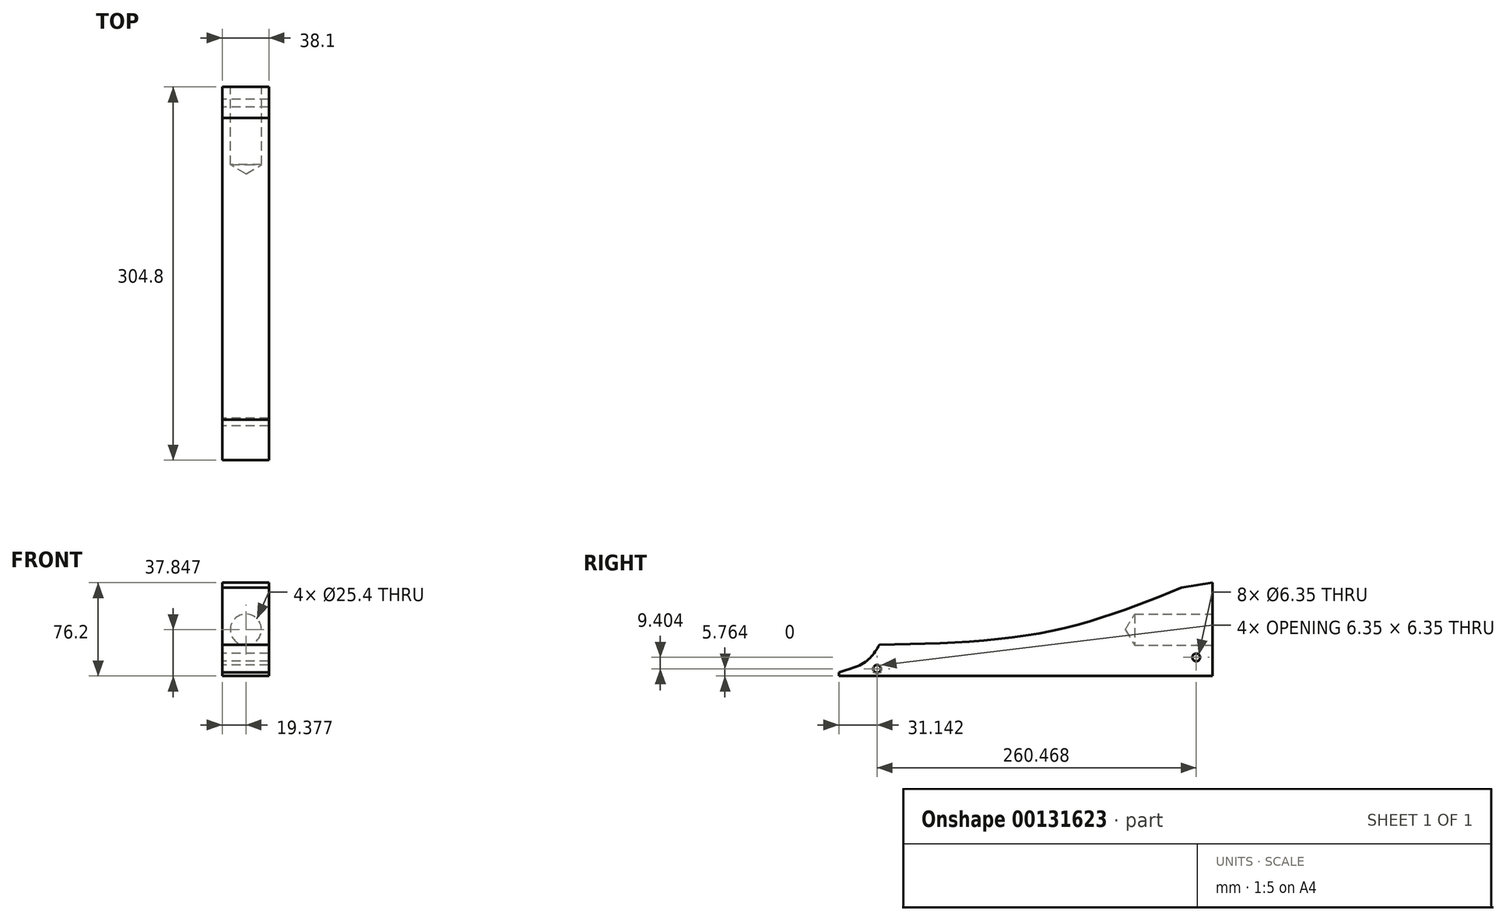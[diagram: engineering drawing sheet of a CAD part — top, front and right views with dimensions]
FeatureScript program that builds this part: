
annotation { "Feature Type Name" : "Feature", "Feature Type Description" : "" }
export const myFeature = defineFeature(function(context is Context, id is Id, definition is map)
    precondition{}
    {
        {
            var Q0;
            Q0=qCreatedBy(makeId("Right.planeOp"),FACE);
            var sketch = newSketch(context, id + "F0", { "sketchPlane" : qUnion([Q0])});
            skLineSegment(sketch, "E0", {"start": v(-61.93, -29.35) * mm, "end": v(-61.93, -54.75) * mm});
            skLineSegment(sketch, "E1", {"start": v(-61.93, -54.75) * mm, "end": v(242.87, -54.75) * mm});
            skLineSegment(sketch, "E2", {"start": v(242.87, -54.75) * mm, "end": v(242.87, 21.45) * mm});
            skLineSegment(sketch, "E3", {"start": v(242.87, 21.45) * mm, "end": v(-61.93, -29.35) * mm});
            skSolve(sketch);
        }
        {
            var Q0;
            Q0=makeQuery(id+"F0.imprint","IMPRINT",FACE,{"disambiguationData":[TD([[makeQuery(id+"F0.imprint","IMPRINT",EDGE,{"derivedFrom":sQuery(id+"F0.wireOp",EDGE,"E0")}),1.0]])]});
            extrude(context, id + "F1", {"entities" : qUnion([Q0]), "endBound" : BoundingType.SYMMETRIC, "depth" : 38.1 * mm});
        }
        {
            var Q0;
            Q0=makeQuery(id+"F1.opExtrude","SWEPT_FACE",FACE,{"disambiguationData":[OSD([sQuery(id+"F0.wireOp",EDGE,"E2")])]});
            var sketch = newSketch(context, id + "F2", { "sketchPlane" : qUnion([Q0])});
            skPoint(sketch, "E4", {"position": v(-0.33, -16.9) * mm});
            skSolve(sketch);
        }
        {
            var Q0;
            Q0=sQuery(id+"F2.wireOp",VERTEX,"E4");
            var Q1;
            Q1=makeQuery(id+"F1.opExtrude","SWEPT_BODY",BODY,{"disambiguationData":[OSD([sQuery(id+"F0.wireOp",EDGE,"E0"),sQuery(id+"F0.wireOp",EDGE,"E1"),sQuery(id+"F0.wireOp",EDGE,"E2"),sQuery(id+"F0.wireOp",EDGE,"E3")])]});
            hole(context, id + "F3", {"style" : HoleStyle.SIMPLE, "endStyle" : HoleEndStyle.BLIND, "holeDiameter" : 25.4 * mm, "holeDepth" : 63.5 * mm, "locations" : qUnion([Q0]), "scope" : qUnion([Q1])});
        }
        {
            var Q0;
            Q0=makeQuery(id+"F1.opExtrude","CAP_FACE",FACE,{"disambiguationData":[OSD([sQuery(id+"F0.wireOp",EDGE,"E0"),sQuery(id+"F0.wireOp",EDGE,"E1"),sQuery(id+"F0.wireOp",EDGE,"E2"),sQuery(id+"F0.wireOp",EDGE,"E3")])],"isStart":true});
            var sketch = newSketch(context, id + "F4", { "sketchPlane" : qUnion([Q0])});
            skFitSpline(sketch, "E5", {"points": [v(-217.43, 17.21) * mm, v(-104.02, -19.52) * mm, v(61.93, -29.35) * mm], "startDerivative": vector(233.78, -94.31) * mm, "endDerivative": vector(322.5, -1.38) * mm});
            skSolve(sketch);
        }
        {
            var Q0;
            {var subQ0=sQuery(id+"F4.wireOp",EDGE,"E5");Q0=makeQuery(id+"F4.imprint","IMPRINT",FACE,{"disambiguationData":[TD([[makeQuery(id+"F4.imprint","IMPRINT",EDGE,{"derivedFrom":subQ0}),1.0]])]});}
            extrude(context, id + "F5", {"entities" : qUnion([Q0]), "operationType" : NewBodyOperationType.REMOVE, "oppositeDirection" : true, "depth" : 50.5 * mm});
        }
        {
            var Q0;
            Q0=makeQuery(id+"F1.opExtrude","CAP_FACE",FACE,{"disambiguationData":[OSD([sQuery(id+"F0.wireOp",EDGE,"E0"),sQuery(id+"F0.wireOp",EDGE,"E1"),sQuery(id+"F0.wireOp",EDGE,"E2"),sQuery(id+"F0.wireOp",EDGE,"E3")])],"isStart":true});
            var sketch = newSketch(context, id + "F6", { "sketchPlane" : qUnion([Q0])});
            skFitSpline(sketch, "E6", {"points": [v(61.93, -51.73) * mm, v(39.84, -42.94) * mm, v(28.78, -29.15) * mm], "startDerivative": vector(-45.85, 12.74) * mm, "endDerivative": vector(-19.82, 33.2) * mm});
            skSolve(sketch);
        }
        {
            var Q0;
            {var subQ0=sQuery(id+"F6.wireOp",EDGE,"E6");Q0=makeQuery(id+"F6.imprint","IMPRINT",FACE,{"disambiguationData":[TD([[makeQuery(id+"F6.imprint","IMPRINT",EDGE,{"derivedFrom":subQ0}),-1.0]])]});}
            extrude(context, id + "F7", {"entities" : qUnion([Q0]), "operationType" : NewBodyOperationType.REMOVE, "oppositeDirection" : true, "depth" : 40.62 * mm});
        }
        {
            var Q0;
            Q0=makeQuery(id+"F1.opExtrude","CAP_FACE",FACE,{"disambiguationData":[OSD([sQuery(id+"F0.wireOp",EDGE,"E0"),sQuery(id+"F0.wireOp",EDGE,"E1"),sQuery(id+"F0.wireOp",EDGE,"E2"),sQuery(id+"F0.wireOp",EDGE,"E3")])],"isStart":true});
            var sketch = newSketch(context, id + "F8", { "sketchPlane" : qUnion([Q0])});
            skPoint(sketch, "E7", {"position": v(30.79, -48.99) * mm});
            skSolve(sketch);
        }
        {
            var Q0;
            Q0=sQuery(id+"F8.wireOp",VERTEX,"E7");
            var Q1;
            Q1=makeQuery(id+"F1.opExtrude","SWEPT_BODY",BODY,{"disambiguationData":[OSD([sQuery(id+"F0.wireOp",EDGE,"E0"),sQuery(id+"F0.wireOp",EDGE,"E1"),sQuery(id+"F0.wireOp",EDGE,"E2"),sQuery(id+"F0.wireOp",EDGE,"E3")])]});
            hole(context, id + "F9", {"style" : HoleStyle.SIMPLE, "endStyle" : HoleEndStyle.THROUGH, "holeDiameter" : 6.35 * mm, "locations" : qUnion([Q0]), "scope" : qUnion([Q1]), "isTappedThrough" : true});
        }
        {
            var Q0;
            Q0=makeQuery(id+"F1.opExtrude","CAP_FACE",FACE,{"disambiguationData":[OSD([sQuery(id+"F0.wireOp",EDGE,"E0"),sQuery(id+"F0.wireOp",EDGE,"E1"),sQuery(id+"F0.wireOp",EDGE,"E2"),sQuery(id+"F0.wireOp",EDGE,"E3")])],"isStart":true});
            var sketch = newSketch(context, id + "F10", { "sketchPlane" : qUnion([Q0])});
            skPoint(sketch, "E8", {"position": v(-229.68, -39.58) * mm});
            skSolve(sketch);
        }
        {
            var Q0;
            Q0=sQuery(id+"F10.wireOp",VERTEX,"E8");
            var Q1;
            Q1=makeQuery(id+"F1.opExtrude","SWEPT_BODY",BODY,{"disambiguationData":[OSD([sQuery(id+"F0.wireOp",EDGE,"E0"),sQuery(id+"F0.wireOp",EDGE,"E1"),sQuery(id+"F0.wireOp",EDGE,"E2"),sQuery(id+"F0.wireOp",EDGE,"E3")])]});
            hole(context, id + "F11", {"style" : HoleStyle.SIMPLE, "endStyle" : HoleEndStyle.THROUGH, "holeDiameter" : 6.35 * mm, "locations" : qUnion([Q0]), "scope" : qUnion([Q1]), "isTappedThrough" : true});
        }
    });
